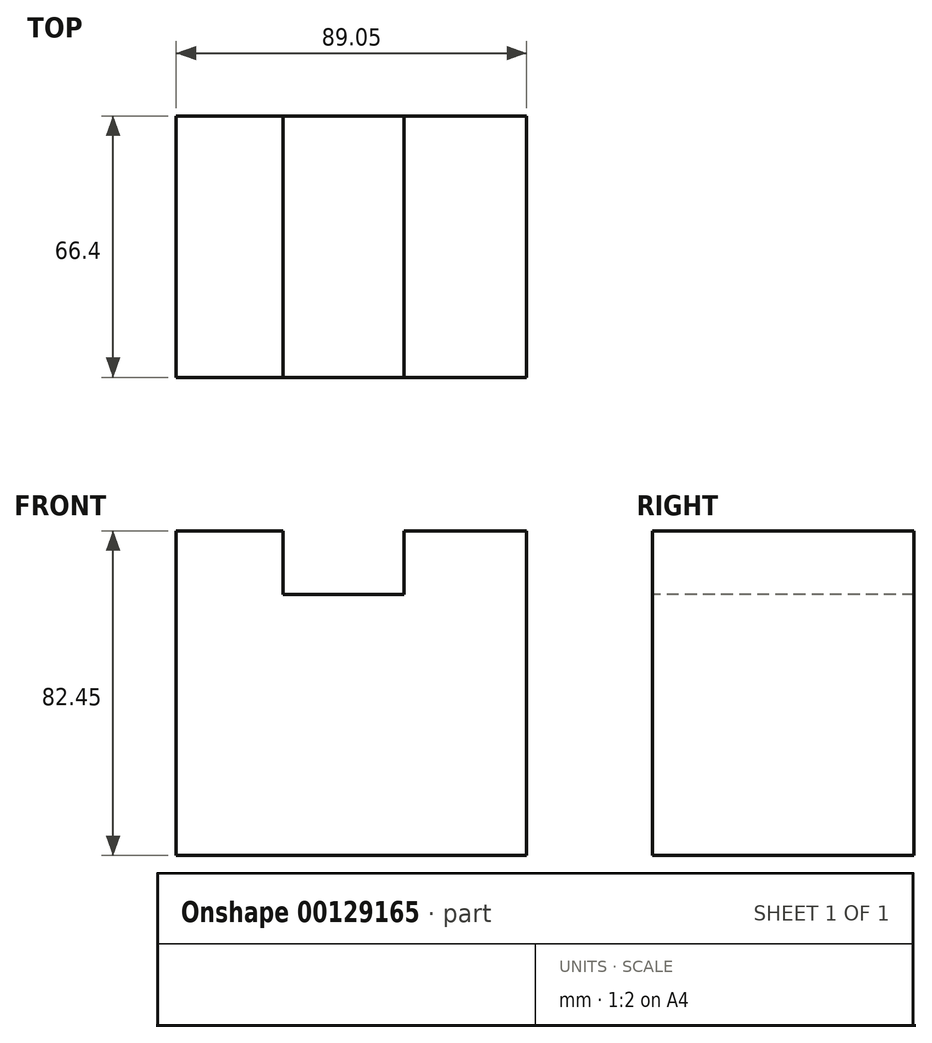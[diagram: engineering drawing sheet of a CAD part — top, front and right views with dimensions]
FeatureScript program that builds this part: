
annotation { "Feature Type Name" : "Feature", "Feature Type Description" : "" }
export const myFeature = defineFeature(function(context is Context, id is Id, definition is map)
    precondition{}
    {
        {
            var Q0;
            Q0=qCreatedBy(makeId("Front.planeOp"),FACE);
            var sketch = newSketch(context, id + "F0", { "sketchPlane" : qUnion([Q0])});
            skLineSegment(sketch, "E0.top", {"start": v(0, -82.45) * mm, "end": v(-89.05, -82.45) * mm});
            skLineSegment(sketch, "E0.left", {"start": v(0, 0) * mm, "end": v(0, -82.45) * mm});
            skLineSegment(sketch, "E0.right", {"start": v(-89.05, 0) * mm, "end": v(-89.05, -82.45) * mm});
            skLineSegment(sketch, "E1.top", {"start": v(-61.9, -16.13) * mm, "end": v(-31.13, -16.13) * mm});
            skLineSegment(sketch, "E1.left", {"start": v(-61.9, 0) * mm, "end": v(-61.9, -16.13) * mm});
            skLineSegment(sketch, "E1.right", {"start": v(-31.13, 0) * mm, "end": v(-31.13, -16.13) * mm});
            skLineSegment(sketch, "E2", {"start": v(-89.05, 0) * mm, "end": v(-61.9, 0) * mm});
            skLineSegment(sketch, "E3", {"start": v(0, 0) * mm, "end": v(-31.13, 0) * mm});
            skSolve(sketch);
        }
        {
            var Q0;
            Q0 = qSketchRegion(id + "F0", true);
            extrude(context, id + "F1", {"entities" : qUnion([Q0]), "oppositeDirection" : true, "depth" : 66.4 * mm});
        }
    });
